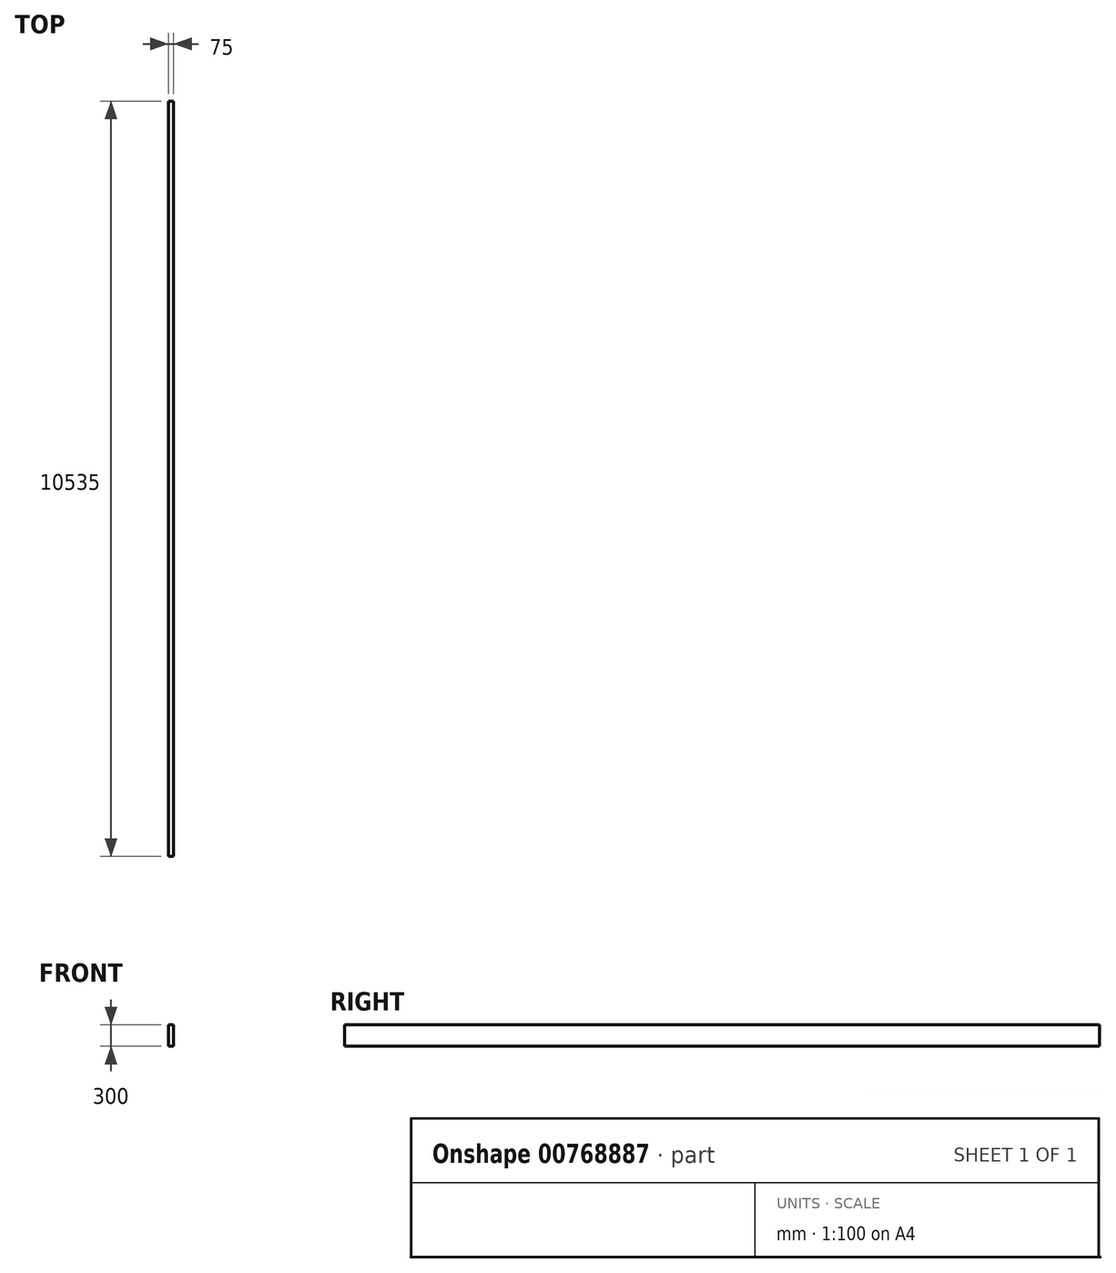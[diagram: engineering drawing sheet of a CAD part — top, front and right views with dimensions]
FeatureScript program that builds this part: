
annotation { "Feature Type Name" : "Feature", "Feature Type Description" : "" }
export const myFeature = defineFeature(function(context is Context, id is Id, definition is map)
    precondition{}
    {
        {
            var Q0;
            Q0=qCreatedBy(makeId("Front.planeOp"),FACE);
            var sketch = newSketch(context, id + "F0", { "sketchPlane" : qUnion([Q0])});
            skLineSegment(sketch, "E0.bottom", {"start": v(37.5, -150) * mm, "end": v(-37.5, -150) * mm});
            skLineSegment(sketch, "E0.top", {"start": v(37.5, 150) * mm, "end": v(-37.5, 150) * mm});
            skLineSegment(sketch, "E0.left", {"start": v(37.5, -150) * mm, "end": v(37.5, 150) * mm});
            skLineSegment(sketch, "E0.right", {"start": v(-37.5, -150) * mm, "end": v(-37.5, 150) * mm});
            skPoint(sketch, "E0.middle", {"position": v(0, 0) * mm});
            skSolve(sketch);
        }
        {
            var Q0;
            Q0=makeQuery(id+"F0.imprint","IMPRINT",FACE,{"disambiguationData":[TD([[makeQuery(id+"F0.imprint","IMPRINT",EDGE,{"derivedFrom":sQuery(id+"F0.wireOp",EDGE,"E0.bottom")}),-1.0]])]});
            extrude(context, id + "F1", {"entities" : qUnion([Q0]), "depth" : 10535 * mm, "offsetDistance" : 25 * mm});
        }
    });
